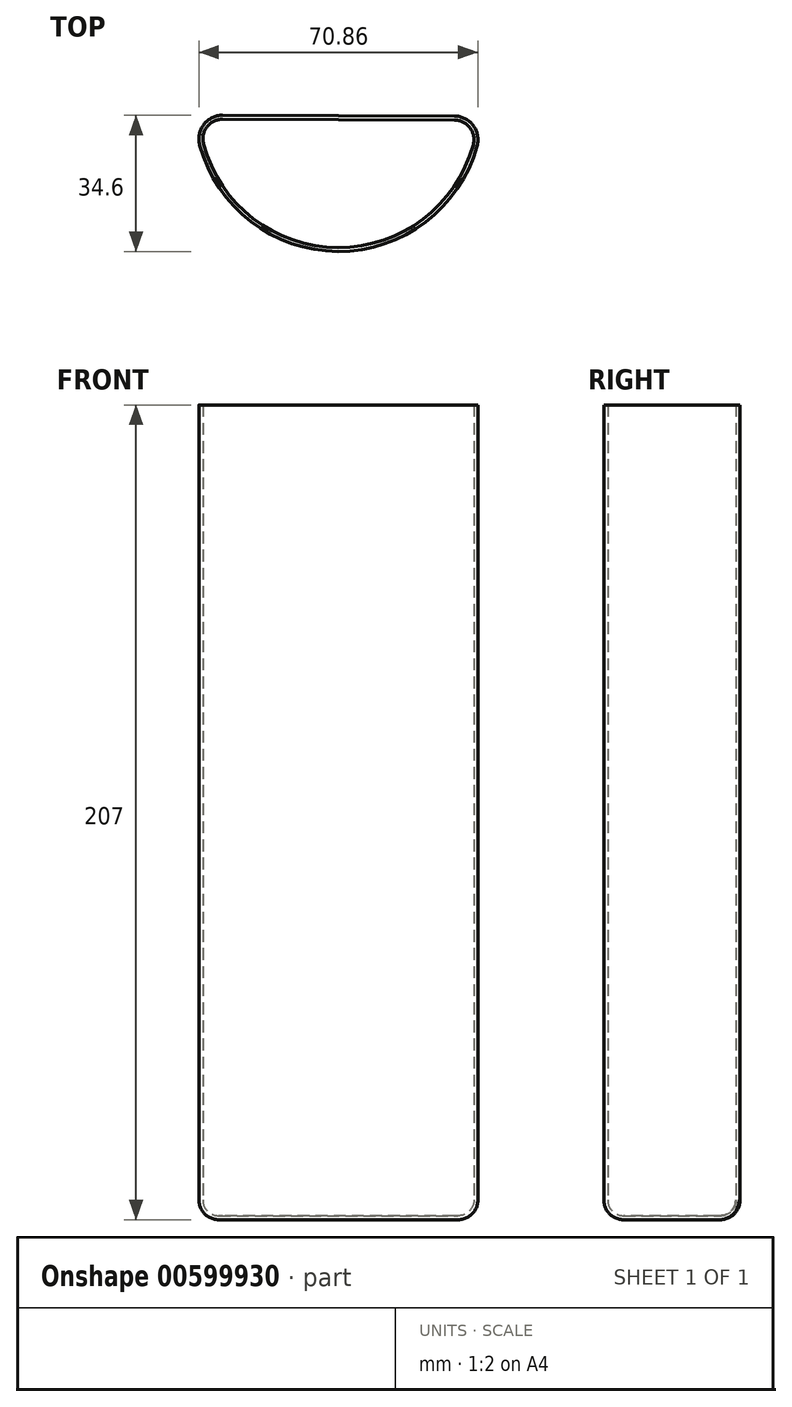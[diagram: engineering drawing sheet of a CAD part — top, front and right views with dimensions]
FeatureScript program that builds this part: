
annotation { "Feature Type Name" : "Feature", "Feature Type Description" : "" }
export const myFeature = defineFeature(function(context is Context, id is Id, definition is map)
    precondition{}
    {
        {
            var Q0;
            Q0=qCreatedBy(makeId("Top.planeOp"),FACE);
            var sketch = newSketch(context, id + "F0", { "sketchPlane" : qUnion([Q0])});
            skArc(sketch, "E0", {"start": v(-35.26, -9.45) * mm, "mid": v(-0.13, -36.5) * mm, "end": v(35.19, -9.7) * mm});
            skLineSegment(sketch, "E1", {"start": v(-29.44, -1.9) * mm, "end": v(29.42, -2.1) * mm});
            skPoint(sketch, "E2.visualSharp", {"position": v(-36.45, -1.87) * mm});
            skArc(sketch, "E2.filletArc", {"start": v(-29.44, -1.9) * mm, "mid": v(-34.21, -4.24) * mm, "end": v(-35.26, -9.45) * mm});
            skPoint(sketch, "E3.visualSharp", {"position": v(36.44, -2.13) * mm});
            skArc(sketch, "E3.filletArc", {"start": v(35.19, -9.7) * mm, "mid": v(34.18, -4.48) * mm, "end": v(29.42, -2.1) * mm});
            skSolve(sketch);
        }
        {
            var Q0;
            Q0=makeQuery(id+"F0.imprint","IMPRINT",FACE,{"disambiguationData":[TD([[makeQuery(id+"F0.imprint","IMPRINT",EDGE,{"derivedFrom":sQuery(id+"F0.wireOp",EDGE,"E0")}),1.0]])]});
            var Q1;
            Q1=sQuery(id+"F0.wireOp",EDGE,"E1");
            var Q2;
            Q2 = qBodyType(qCreatedBy(id + "F0" ,EDGE), BodyType.WIRE);
            extrude(context, id + "F1", {"entities" : qUnion([Q0]), "surfaceEntities" : qUnion([Q1, Q2]), "depth" : 207 * mm, "offsetDistance" : 25 * mm});
        }
        {
            var Q0;
            Q0=makeQuery(id+"F1.opExtrude","CAP_EDGE",EDGE,{"disambiguationData":[OSD([sQuery(id+"F0.wireOp",EDGE,"E0")])],"isStart":true});
            fillet(context, id + "F2", {"entities" : qUnion([Q0]), "radius" : 5 * mm, "tangentPropagation" : true, "allowEdgeOverflow" : false});
        }
        {
            var Q0;
            Q0=makeQuery(id+"F1.opExtrude","CAP_FACE",FACE,{"disambiguationData":[OSD([sQuery(id+"F0.wireOp",EDGE,"E0"),sQuery(id+"F0.wireOp",EDGE,"E1"),sQuery(id+"F0.wireOp",EDGE,"E2.filletArc"),sQuery(id+"F0.wireOp",EDGE,"E3.filletArc")])],"isStart":false});
            shell(context, id + "F3", {"entities" : qUnion([Q0]), "thickness" : 1 * mm});
        }
    });
